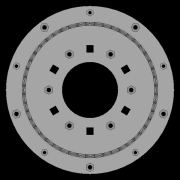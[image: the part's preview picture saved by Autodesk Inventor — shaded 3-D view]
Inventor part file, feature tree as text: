
AUTODESK INVENTOR PART (.ipt)
format: ipt  version: 2022.2 (Build 262287010, 287A)  size: 1,540,096 bytes
history: native  units: mm
features: extrude x28, other x19, sketch x17, pattern_circular x11, plane x4, fillet x2, move_body x2, revolve x2, draft x2, chamfer x2
ambient origin geometry x8: Origin, YZ Plane, XZ Plane, XY Plane, X Axis, Y Axis, Z Axis, Center Point
bodies: Solid5 (feature_tree)
feature tree (89):
  other  "CrossSection1"
  sketch  "Sketch7"  dims[d167=8.972256mm]
  other  "Roller1"
  other  "Roller2"
  sketch  "Sketch22"  dims[d173=10.814812mm]
  sketch  "Sketch2"  dims[d57=4.025mm d90=61.984365mm]
  sketch  "Sketch23"  dims[d201=75.0mm d232=0.0mm d233=3600.0mm]
  other  "RevRoller1"
  fillet  "Fillet1"  Radius=59.246882mm
  extrude  "Extrusion39"  Depth=61.984365mm
  pattern_circular  "Circular Pattern13"  Count=360  [1 undecoded]
  move_body  "Move Body7"
  revolve  "Revolution13"  [1 undecoded]
  fillet  "Fillet3"  Radius=0.025mm
  pattern_circular  "Circular Pattern14"  Count=24  [1 undecoded]
  move_body  "Move Body6"
  revolve  "Revolution14"  Angle=360.0deg
  other  "OuterRim_Top2"
  other  "OuterRim_Bottom2"
  plane  "Work Plane8"
  sketch  "Sketch49"  dims[d352=0.025mm]
  sketch  "Sketch50"  dims[d354=0.025mm]
  sketch  "Sketch51"  dims[d355=16.1595mm]
  extrude  "Extrusion40"  Depth=0.5mm
  extrude  "Extrusion41"  Depth=0.5mm
  extrude  "Extrusion42"  Depth=0.5mm
  extrude  "Extrusion43"  Depth=1.0mm
  sketch  "Sketch52"  dims[d356=16.159664mm]
  extrude  "Extrusion44"  Depth=0.5mm
  extrude  "Extrusion45"  TaperAngle=90.0deg  [1 undecoded]
  extrude  "Extrusion46"  Depth=0.5mm
  extrude  "Extrusion47"  Depth=0.5mm
  pattern_circular  "Circular Pattern32"  Angle=360.0deg  [1 undecoded]
  pattern_circular  "Circular Pattern33"  Angle=90.0deg  [1 undecoded]
  sketch  "Sketch57"  dims[d358=360.0deg]
  extrude  "Extrusion50"  Depth=0.1mm
  extrude  "Extrusion51"  Depth=0.5mm
  pattern_circular  "Circular Pattern34"  [2 undecoded]
  extrude  "Extrusion52"  Depth=0.5mm
  extrude  "Extrusion53"  Depth=0.5mm
  pattern_circular  "Circular Pattern35"  [2 undecoded]
  plane  "Work Plane7"
  sketch  "Sketch47"  dims[d350=47.575427mm]
  extrude  "Rotor_Ring"  TaperAngle=0.0deg  [1 undecoded]
  draft  "FaceDraft2"
  sketch  "Sketch30"  dims[d343=16.1595mm d344=16.159664mm d345=0.025mm]
  plane  "Work Plane5"
  other  "Rotor Featurs"
  other  "RotorRim_Bottom"
  extrude  "Extrusion24"  TaperAngle=0.0deg  [1 undecoded]
  extrude  "Extrusion25"  Depth=25.0mm
  extrude  "Extrusion26"  Depth=0.5mm
  pattern_circular  "Circular Pattern23"  [2 undecoded]
  sketch  "Sketch41"  dims[d347=0.1mm]
  extrude  "Extrusion27"  Depth=1.5mm
  extrude  "Extrusion28"  Depth=1.5mm
  pattern_circular  "Circular Pattern24"  [2 undecoded]
  extrude  "Extrusion29"  TaperAngle=90.0deg  [1 undecoded]
  extrude  "Extrusion30"  TaperAngle=90.0deg  [1 undecoded]
  extrude  "Extrusion31"  TaperAngle=90.0deg  [1 undecoded]
  pattern_circular  "Circular Pattern25"  [2 undecoded]
  sketch  "Sketch42"  dims[d348=0.1mm]
  extrude  "Extrusion32"  Depth=11.193516mm
  extrude  "Extrusion33"  TaperAngle=0.0deg  [1 undecoded]
  extrude  "Extrusion34"  Depth=0.5mm
  extrude  "Extrusion35"  Depth=0.5mm TaperAngle=0.0deg
  pattern_circular  "Circular Pattern26"  [2 undecoded]
  pattern_circular  "Circular Pattern27"  [2 undecoded]
  chamfer  "Chamfer1"  Distance=8.0mm
  chamfer  "Chamfer2"  Distance=2.5mm Angle=30.0deg
  draft  "FaceDraft4"
  plane  "Work Plane6"
  sketch  "Sketch43"  dims[d349=47.575591mm]
  extrude  "Extrusion37"  Depth=0.5mm
  extrude  "Extrusion38"  Depth=0.5mm TaperAngle=30.0deg
  other  "2D Equation Curve1"
  sketch  "Sketch40"  dims[d346=0.025mm]
  other  "Work Axis6"
  other  "Work Axis7"
  other  "Work Axis8"
  other  "Work Axis9"
  other  "Work Axis10"
  other  "Work Point1"
  other  "Work Point2"
  other  "Work Point3"
  other  "Work Point4"
  other  "Work Point5"
  sketch  "Sketch48"  dims[d351=0.025mm]
  sketch  "Sketch58"  dims[d359=0.5mm d360=240.0mm d361=360.0deg d363=1.308997mm d367=8.1mm d370=0.025mm d371=1.0mm d372=1.308997mm d373=90.0deg d374=0.5mm d375=240.0mm d376=360.0deg d378=90.0deg d379=0.1mm d380=0.025mm d381=0.025mm d382=0.025mm d383=0.025mm d384=11.193516mm d385=0.0mm d386=0.0mm d391=25.0mm d392=75.0mm d393=1.5mm d394=1.5mm d395=1.5mm d396=1.5mm d397=90.0deg d398=90.0deg d399=90.0deg d400=75.0mm d401=11.193516mm d402=0.0mm d486=0.436332mm d487=0.5mm d488=2.0mm d489=0.0mm d490=20.0mm d495=2.5mm d496=8.0mm d506=13.856406mm d507=55.5mm d508=8.0mm d509=0.05mm d510=2.5mm d511=30.0deg d512=12.0mm d513=6.0mm d514=0.2mm d515=30.0deg d516=131.0mm d517=65.5mm d518=0.2mm d519=100.0mm d520=120.0mm d521=2.0mm d522=150.0mm d530=50.0mm d531=5.5mm d532=5.5mm d533=5.5mm d534=85.75mm d535=73.5mm d536=61.25mm d537=24.5mm d538=3.0mm d539=2.4mm d540=0.0mm d541=0.0mm d542=0.0mm d543=5.5mm d544=3.0mm d545=0.0mm d546=90.0mm d547=360.0deg d549=3.0mm d550=3.0mm d551=2.4mm d552=0.0mm d553=5.596758mm d554=0.0mm d555=2.4mm d556=0.0mm d557=5.596758mm d558=0.0mm d559=5.596758mm d560=0.0mm d561=90.0mm d562=360.0deg d564=60.0mm d565=360.0deg d567=5.5mm d568=5.5mm d569=3.0mm d570=0.0mm d571=5.596758mm d572=0.0mm d573=3.0mm d574=0.0mm d575=5.596758mm d576=0.0mm d577=90.0mm d578=360.0deg d580=60.0mm d581=360.0deg d584=20.0mm d585=8.0mm d587=1.75mm d589=3.0mm d592=2.0mm d593=12.0mm d594=12.0mm d600=0.5mm d601=2.0mm d602=45.0deg d603=0.5mm d604=2.0mm d605=45.0deg d606=0.436332mm d607=0.5mm d608=0.0mm d609=20.0mm d611=360.0deg d613=0.0mm d614=0.0mm d617=0.99971mm d618=100.0mm d620=69.0mm d621=5.0mm d622=0.5mm d623=0.5mm d624=5.0mm d625=0.2mm d626=0.0mm d627=20.0mm d629=69.0mm d630=73.5mm d631=20.0mm d633=6.283185mm d635=5.5mm d636=3.0mm d637=7.0mm d638=4.0mm d639=5.596758mm d640=0.0mm d641=3.0mm d642=0.0mm d643=5.596758mm d644=0.0mm d645=4.0mm d646=0.0mm d647=20.0mm d649=6.283185mm d651=3.0mm d652=4.0mm d653=20.0mm d655=6.283185mm d657=7.0mm d658=5.5mm d659=5.596758mm d660=0.0mm d661=2.593516mm d662=0.0mm d663=5.596758mm d664=0.0mm d665=3.193516mm d666=0.0mm d679=50.0mm d680=360.0deg d682=50.0mm d683=360.0deg d694=6.35mm d695=6.35mm d696=6.2mm d697=6.2mm d698=11.194mm d699=0.0mm d700=8.194mm d701=0.0mm d702=60.0mm d703=360.0deg d705=30.0deg d706=4.0mm d707=7.0mm d708=3.193516mm d709=0.0mm d710=11.193516mm d711=0.0mm d712=60.0mm d713=360.0deg d16=0.872665mm d17=0.872665mm d49=0.872665mm d50=0.872665mm d51=0.872665mm d52=0.872665mm d236=0.5mm d237=0.872665mm d238=0.5mm d239=0.872665mm d282=1.0mm d283=1.0mm d284=1.0mm d285=0.15mm d286=0.25mm d287=0.375mm d288=14.3117mm d289=0.75mm d290=20.594885mm d291=0.0625mm d292=0.75mm d293=0.375mm d405=0.5mm d406=0.872665mm d407=0.5mm d408=0.872665mm d413=0.5mm d414=0.872665mm d415=0.5mm d416=0.872665mm d417=0.5mm d418=0.872665mm d419=0.5mm d420=0.872665mm d421=0.872665mm d431=0.5mm d432=0.872665mm d433=0.5mm d434=0.872665mm d471=0.5mm d472=0.872665mm d473=0.5mm d474=0.872665mm d497=0.5mm d498=0.872665mm d499=0.5mm d500=0.872665mm d590=0.5mm d591=0.872665mm]
note: 26 required parameter values undecoded (feature->parameter linkage not recoverable at this tier; creation-order binding heuristic only, values carry confidence <= 0.55)